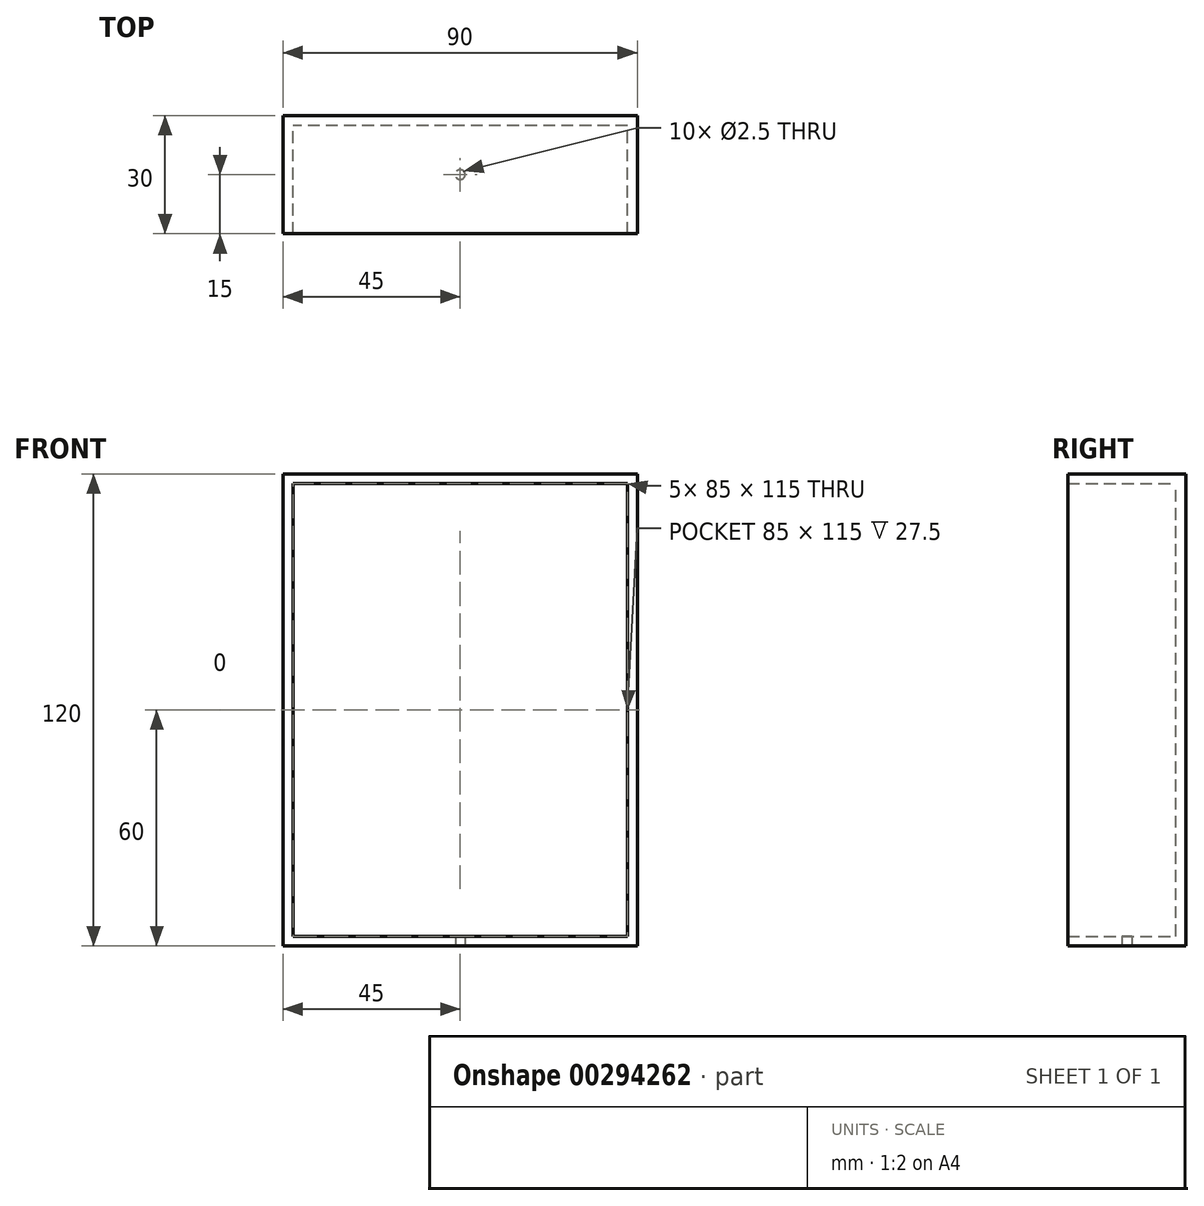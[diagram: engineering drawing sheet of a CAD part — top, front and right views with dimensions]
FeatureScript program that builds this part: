
annotation { "Feature Type Name" : "Feature", "Feature Type Description" : "" }
export const myFeature = defineFeature(function(context is Context, id is Id, definition is map)
    precondition{}
    {
        {
            var Q0;
            Q0=qCreatedBy(makeId("Front.planeOp"),FACE);
            var sketch = newSketch(context, id + "F0", { "sketchPlane" : qUnion([Q0])});
            skLineSegment(sketch, "E0.bottom", {"start": v(0, 0) * mm, "end": v(-90, 0) * mm});
            skLineSegment(sketch, "E0.top", {"start": v(0, 120) * mm, "end": v(-90, 120) * mm});
            skLineSegment(sketch, "E0.left", {"start": v(0, 0) * mm, "end": v(0, 120) * mm});
            skLineSegment(sketch, "E0.right", {"start": v(-90, 0) * mm, "end": v(-90, 120) * mm});
            skSolve(sketch);
        }
        {
            var Q0;
            Q0 = qSketchRegion(id + "F0", true);
            extrude(context, id + "F1", {"entities" : qUnion([Q0]), "depth" : 30 * mm});
        }
        {
            var Q0;
            Q0=makeQuery(id+"F1.opExtrude","CAP_FACE",FACE,{"disambiguationData":[OSD([sQuery(id+"F0.wireOp",EDGE,"E0.bottom"),sQuery(id+"F0.wireOp",EDGE,"E0.top"),sQuery(id+"F0.wireOp",EDGE,"E0.left"),sQuery(id+"F0.wireOp",EDGE,"E0.right")])],"isStart":false});
            shell(context, id + "F2", {"entities" : qUnion([Q0]), "thickness" : 2.5 * mm});
        }
        {
            var Q0;
            Q0=makeQuery(id+"F1.opExtrude","SWEPT_FACE",FACE,{"disambiguationData":[OSD([sQuery(id+"F0.wireOp",EDGE,"E0.bottom")])]});
            var sketch = newSketch(context, id + "F3", { "sketchPlane" : qUnion([Q0])});
            skLineSegment(sketch, "E1", {"start": v(-45, 30) * mm, "end": v(-45, 0) * mm, "construction": true});
            skLineSegment(sketch, "E2", {"start": v(-90, 15) * mm, "end": v(0, 15) * mm, "construction": true});
            skCircle(sketch, "E3", {"center": v(-45, 15) * mm, "radius": 1.25 * mm});
            skSolve(sketch);
        }
        {
            var Q0;
            Q0=makeQuery(id+"F3.imprint","IMPRINT",FACE,{"disambiguationData":[TD([[makeQuery(id+"F3.imprint","IMPRINT",EDGE,{"derivedFrom":sQuery(id+"F3.wireOp",EDGE,"E3")}),1.0]])]});
            extrude(context, id + "F4", {"entities" : qUnion([Q0]), "operationType" : NewBodyOperationType.REMOVE, "oppositeDirection" : true, "depth" : 25 * mm});
        }
    });
